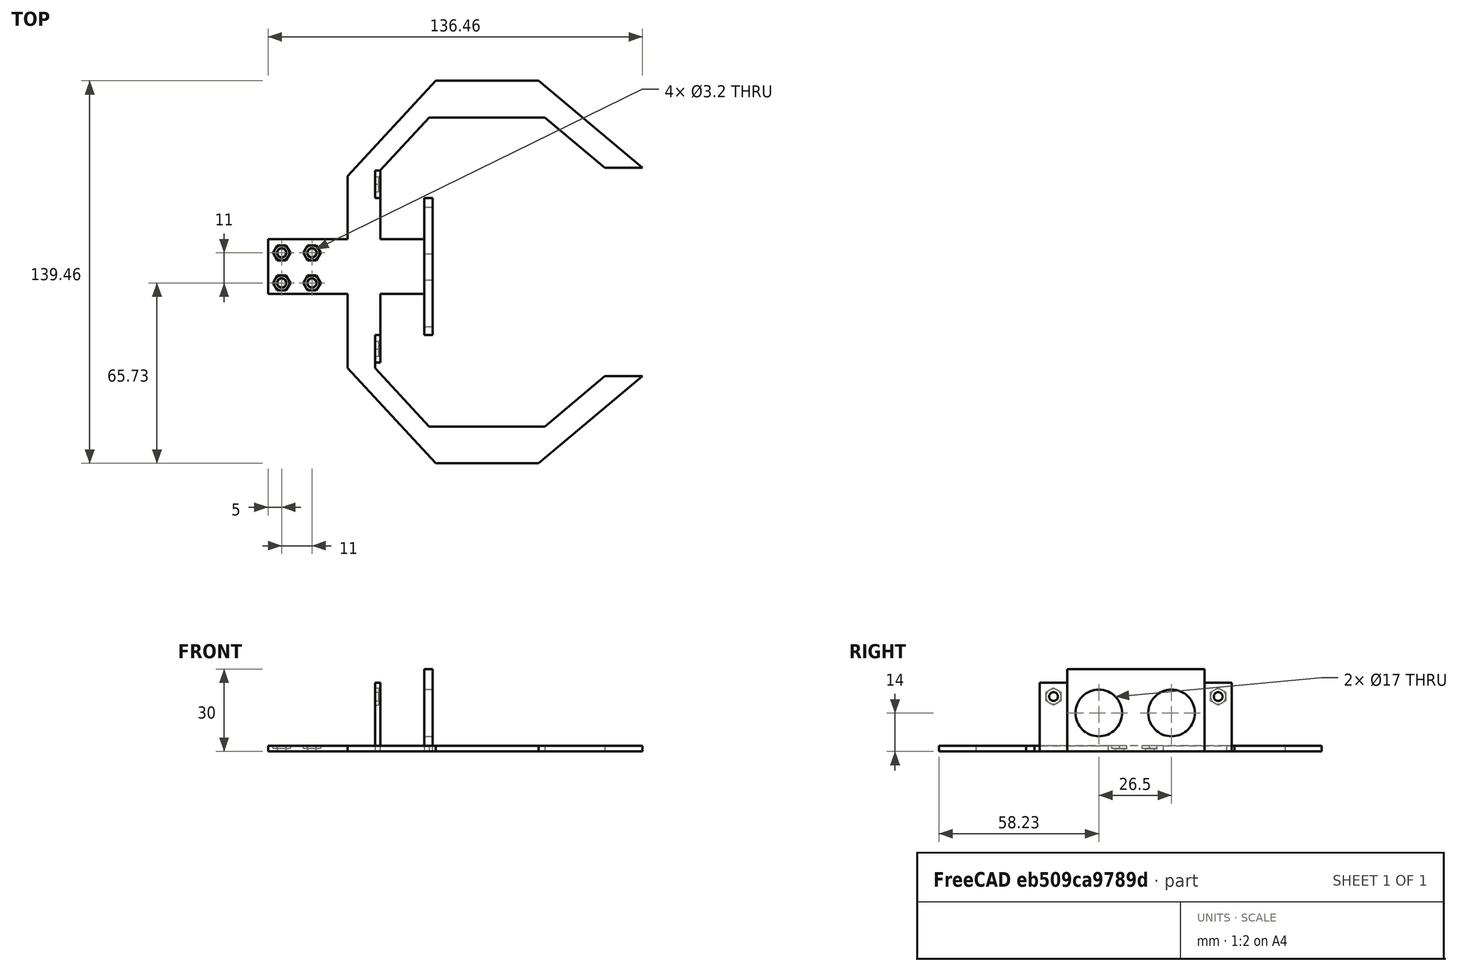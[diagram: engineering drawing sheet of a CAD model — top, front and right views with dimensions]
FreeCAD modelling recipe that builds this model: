
FCSTD DOCUMENT  (FreeCAD 0.21R33771 (Git))
Label: soporteSensoresCuernos
License: All rights reserved
LicenseURL: http://en.wikipedia.org/wiki/All_rights_reserved
objects: Part::MultiFuse×9, Part::Cylinder×8, Part::FeaturePython×6, Part::Box×5, Part::Cut×4, Sketcher::SketchObject×1, PartDesign::Pad×1, PartDesign::Body×1, Mesh::Feature×1
note: 36 computed .brp shape members not serialized (recipe doc carries the construction recipe); baked Part::Feature solids carry a one-line shape summary decoded from their .brp

FEATURE [Part::Box] Box028  label="Cubo028"
  AttacherType = Attacher::AttachEngine3D
  Height = 2
  Length = 60
  Placement = pos=(21,-10,-11) rot=(0,0,1;0rad)
  Width = 20
FEATURE [Part::Box] Box030  label="Cubo030"
  AttacherType = Attacher::AttachEngine3D
  Height = 30
  Length = 3
  Placement = pos=(78,-25,-11) rot=(0,0,1;0rad)
  Width = 50
FEATURE [Part::Box] Box031  label="Cubo031"
  AttacherType = Attacher::AttachEngine3D
  Height = 2
  Length = 10
  Placement = pos=(52,-35,-11) rot=(0,0,1;0rad)
  Width = 70
FEATURE [Part::Box] Box032  label="Cubo032"
  AttacherType = Attacher::AttachEngine3D
  Height = 25
  Length = 2
  Placement = pos=(60,-35,-11) rot=(0,0,1;0rad)
  Width = 10
FEATURE [Part::Box] Box033  label="Cubo033"
  AttacherType = Attacher::AttachEngine3D
  Height = 25
  Length = 2
  Placement = pos=(60,-35,-11) rot=(0,0,1;0rad)
  Width = 10
FEATURE [Part::Cylinder] Cylinder083  label="Cilindro083"
  Angle = 360
  AttacherType = Attacher::AttachEngine3D
  FirstAngle = 0
  Height = 10
  Placement = pos=(26,5,-18) rot=(0,0,1;0rad)
  Radius = 1.6
  SecondAngle = 0
FEATURE [Part::Cylinder] Cylinder084  label="Cilindro084"
  Angle = 360
  AttacherType = Attacher::AttachEngine3D
  FirstAngle = 0
  Height = 10
  Placement = pos=(26,-6,-18) rot=(0,0,1;0rad)
  Radius = 1.6
  SecondAngle = 0
FEATURE [Part::Cylinder] Cylinder085  label="Cilindro085"
  Angle = 360
  AttacherType = Attacher::AttachEngine3D
  FirstAngle = 0
  Height = 10
  Placement = pos=(37,-6,-18) rot=(0,0,1;0rad)
  Radius = 1.6
  SecondAngle = 0
FEATURE [Part::Cylinder] Cylinder086  label="Cilindro086"
  Angle = 360
  AttacherType = Attacher::AttachEngine3D
  FirstAngle = 0
  Height = 10
  Placement = pos=(37,5,-18) rot=(0,0,1;0rad)
  Radius = 1.6
  SecondAngle = 0
FEATURE [Part::Cylinder] Cylinder087  label="Cilindro087"
  Angle = 360
  AttacherType = Attacher::AttachEngine3D
  FirstAngle = 0
  Height = 10
  Placement = pos=(75,-13.5,3) rot=(0,1,0;1.5708rad)
  Radius = 8.5
  SecondAngle = 0
FEATURE [Part::Cylinder] Cylinder088  label="Cilindro088"
  Angle = 360
  AttacherType = Attacher::AttachEngine3D
  FirstAngle = 0
  Height = 11
  Placement = pos=(75,13,3) rot=(0,1,0;1.5708rad)
  Radius = 8.5
  SecondAngle = 0
FEATURE [Part::Cylinder] Cylinder089  label="Cilindro089"
  Angle = 360
  AttacherType = Attacher::AttachEngine3D
  FirstAngle = 0
  Height = 10
  Placement = pos=(57,-31,-4) rot=(0,1,0;1.5708rad)
  Radius = 1.6
  SecondAngle = 0
FEATURE [Part::Cylinder] Cylinder090  label="Cilindro090"
  Angle = 360
  AttacherType = Attacher::AttachEngine3D
  FirstAngle = 0
  Height = 10
  Placement = pos=(57,-31,-4) rot=(0,1,0;1.5708rad)
  Radius = 1.6
  SecondAngle = 0
FEATURE [Part::MultiFuse] Fusion042
  Shapes = -> [Cylinder086,Cylinder083,Cylinder084,Cylinder085]
FEATURE [Part::MultiFuse] Fusion043
  Shapes = -> [Cylinder088,Cylinder087]
FEATURE [Part::Cut] Cut023
  Base = -> Box030
  Tool = -> Fusion043
FEATURE [Part::MultiFuse] Fusion044
  Shapes = -> [Box028,Cut023]
FEATURE [Part::FeaturePython] Nut023  label="M3-Tuerca023"  # Fasteners workbench fastener (typed FeaturePython)
  Placement = pos=(59,-31,-4) rot=(0,1,0;1.5708rad)
  diameter = 4
  invert = false
  leftHanded = false
  matchOuter = false
  offset = 0
  thread = false
  type = 22
FEATURE [Part::MultiFuse] Fusion045
  Placement = pos=(0,1,13) rot=(0,0,1;0rad)
  Shapes = -> [Cylinder089,Nut023]
FEATURE [Part::Cut] Cut024
  Base = -> Box032
  Tool = -> Fusion045
FEATURE [Part::FeaturePython] Nut024  label="M3-Tuerca024"  # Fasteners workbench fastener (typed FeaturePython)
  Placement = pos=(59,-31,-4) rot=(0,1,0;1.5708rad)
  diameter = 4
  invert = false
  leftHanded = false
  matchOuter = false
  offset = 0
  thread = false
  type = 22
FEATURE [Part::MultiFuse] Fusion046
  Placement = pos=(0,1,13) rot=(0,0,1;0rad)
  Shapes = -> [Cylinder090,Nut024]
FEATURE [Part::Cut] Cut025
  Base = -> Box033
  Placement = pos=(0,60,0) rot=(0,0,1;0rad)
  Tool = -> Fusion046
FEATURE [Part::MultiFuse] Fusion047
  Shapes = -> [Cut024,Cut025,Box031,Fusion044]
FEATURE [Part::FeaturePython] Nut  label="M3-Tuerca"  # Fasteners workbench fastener (typed FeaturePython)
  Placement = pos=(37,5,-10) rot=(0,0,1;0rad)
  diameter = 4
  invert = false
  leftHanded = false
  matchOuter = false
  offset = 0
  thread = false
  type = 22
FEATURE [Part::FeaturePython] Nut025  label="M3-Tuerca025"  # Fasteners workbench fastener (typed FeaturePython)
  Placement = pos=(37,-6,-10) rot=(0,0,1;0rad)
  diameter = 4
  invert = false
  leftHanded = false
  matchOuter = false
  offset = 0
  thread = false
  type = 22
FEATURE [Part::FeaturePython] Nut026  label="M3-Tuerca026"  # Fasteners workbench fastener (typed FeaturePython)
  Placement = pos=(26,-6,-10) rot=(0,0,1;0rad)
  diameter = 4
  invert = false
  leftHanded = false
  matchOuter = false
  offset = 0
  thread = false
  type = 22
FEATURE [Part::FeaturePython] Nut027  label="M3-Tuerca027"  # Fasteners workbench fastener (typed FeaturePython)
  Placement = pos=(26,5,-10) rot=(0,0,1;0rad)
  diameter = 4
  invert = false
  leftHanded = false
  matchOuter = false
  offset = 0
  thread = false
  type = 22
FEATURE [Part::MultiFuse] Fusion
  Shapes = -> [Nut027,Nut,Nut025,Nut026]
FEATURE [Part::MultiFuse] Fusion048
  Shapes = -> [Fusion042,Fusion]
FEATURE [Part::Cut] Cut  label="soporteSensores"
  Base = -> Fusion047
  Tool = -> Fusion048
FEATURE [Sketcher::SketchObject] Sketch
  FullyConstrained = false
  MapMode = 5
  Support = -> [XY_Plane]
  sketch-geometry (16):
    g0: LineSegment StartX=-35 StartY=10 StartZ=0 EndX=35 EndY=10 EndZ=0
    g1: LineSegment StartX=35 StartY=0 StartZ=0 EndX=-35 EndY=0 EndZ=0
    g2: LineSegment StartX=-35 StartY=10 StartZ=0 EndX=-56.313 EndY=29.7623 EndZ=0
    g3: LineSegment StartX=-56.313 StartY=29.7623 StartZ=0 EndX=-56.313 EndY=71.8799 EndZ=0
    g4: LineSegment StartX=-56.313 StartY=71.8799 StartZ=0 EndX=-37.9592 EndY=93.7308 EndZ=0
    g5: LineSegment StartX=-37.9592 StartY=93.7308 StartZ=0 EndX=-37.9592 EndY=107.459 EndZ=0
    g6: LineSegment StartX=-69.7292 StartY=69.6357 StartZ=0 EndX=-69.7292 EndY=32.2024 EndZ=0
    g7: LineSegment StartX=-69.7292 StartY=32.2024 StartZ=0 EndX=-35 EndY=0 EndZ=0
    g8: LineSegment StartX=-69.7292 StartY=69.6357 StartZ=0 EndX=-37.9592 EndY=107.459 EndZ=0
    g9: LineSegment StartX=35 StartY=10 StartZ=0 EndX=56.313 EndY=29.7623 EndZ=0
    g10: LineSegment StartX=56.313 StartY=29.7623 StartZ=0 EndX=56.313 EndY=71.8799 EndZ=0
    g11: LineSegment StartX=56.313 StartY=71.8799 StartZ=0 EndX=37.9592 EndY=93.7308 EndZ=0
    g12: LineSegment StartX=37.9592 StartY=93.7308 StartZ=0 EndX=37.9592 EndY=107.459 EndZ=0
    g13: LineSegment StartX=37.9592 StartY=107.459 StartZ=0 EndX=69.7292 EndY=69.6357 EndZ=0
    g14: LineSegment StartX=69.7292 StartY=69.6357 StartZ=0 EndX=69.7292 EndY=32.2024 EndZ=0
    g15: LineSegment StartX=69.7292 StartY=32.2024 StartZ=0 EndX=35 EndY=0 EndZ=0
  constraints (31):
    c: Horizontal(g0)
    c: DistanceX(g0,g0) = 70
    c: DistanceY(g1,g0) = 10
    c: Symmetric(g1,g1,g-2)
    c: PointOnObject(g1,g-1)
    c: Coincident(g0,g2)
    c: Coincident(g2,g3)
    c: Coincident(g3,g4)
    c: Coincident(g4,g5)
    c: Vertical(g5)
    c: Coincident(g6,g7)
    c: Coincident(g7,g1)
    c: Vertical(g3)
    c: Vertical(g6)
    c: Parallel(g2,g7)
    c: Coincident(g8,g5)
    c: Coincident(g6,g8)
    c: Parallel(g8,g4)
    c: Coincident(g0,g9)
    c: Coincident(g9,g10)
    c: Coincident(g10,g11)
    c: Coincident(g11,g12)
    c: Coincident(g12,g13)
    c: Coincident(g13,g14)
    c: Coincident(g14,g15)
    c: Symmetric(g2,g9,g-2)
    c: Symmetric(g14,g6,g-2)
    c: Symmetric(g10,g3,g-2)
    c: Symmetric(g13,g6,g-2)
    c: Symmetric(g11,g4,g-2)
    c: Symmetric(g12,g5,g-2)
FEATURE [PartDesign::Pad] Pad
  Direction = (0,0,1)
  Length = 2
  Length2 = 10
  Profile = -> Sketch
  ReferenceAxis = -> Sketch [N_Axis]
  Type = 0
FEATURE [PartDesign::Body] Body
  Group = -> [Sketch,Pad]
  Origin = -> Origin
  Placement = pos=(50,-2,-9) rot=(0.707107,0.707107,0;3.14159rad)
  Tip = -> Pad
FEATURE [Part::MultiFuse] Fusion049
  Shapes = -> [Cut,Body]
FEATURE [Mesh::Feature] Mesh  label="Fusion049 (Meshed)"
